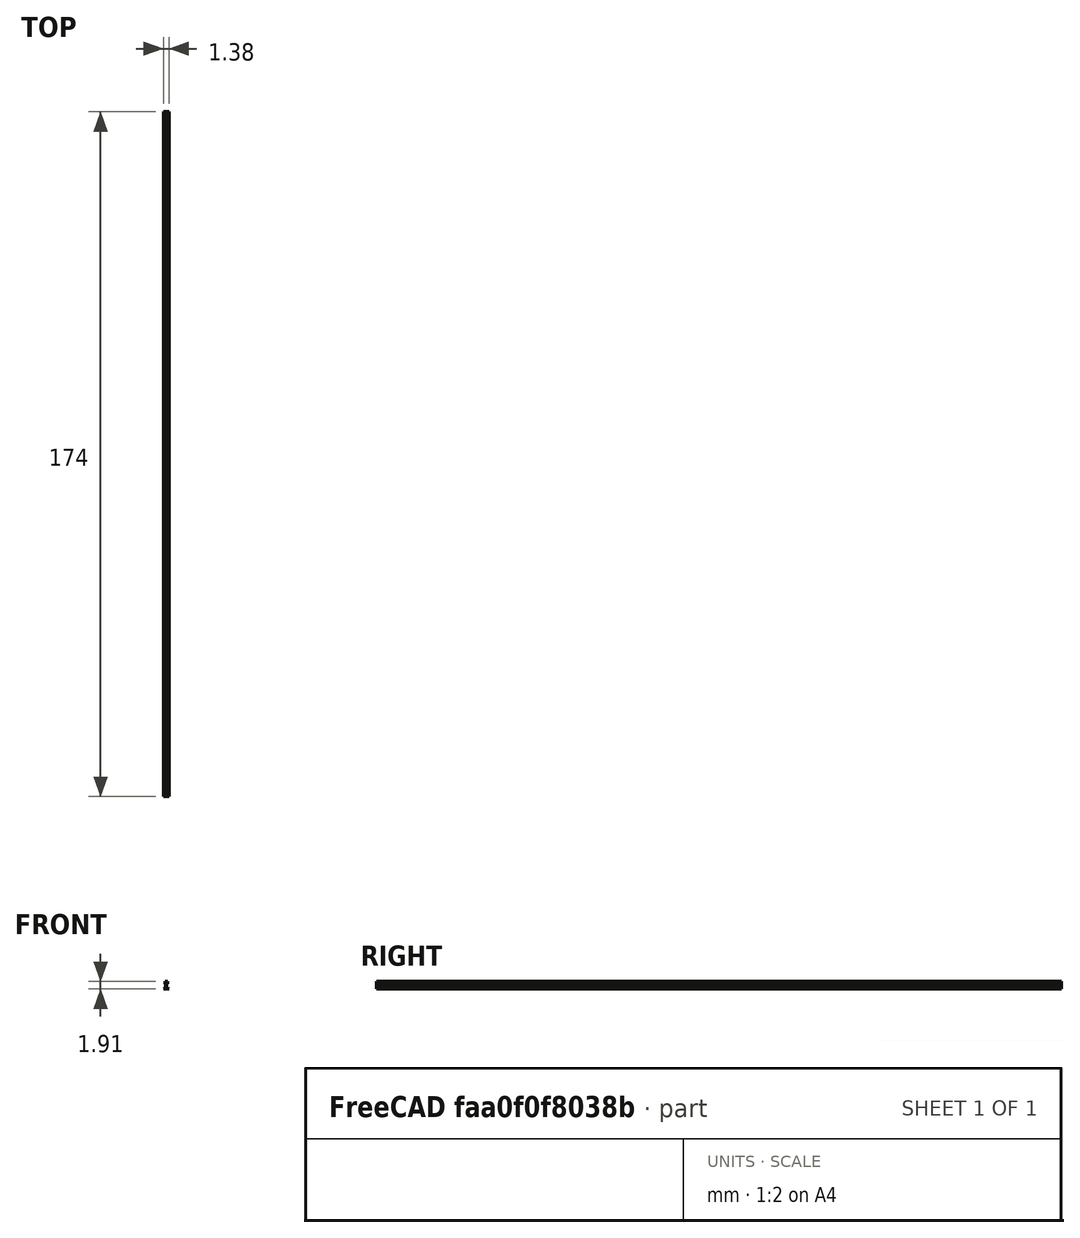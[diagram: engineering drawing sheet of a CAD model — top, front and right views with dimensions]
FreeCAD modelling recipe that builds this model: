
FCSTD DOCUMENT  (FreeCAD 0.18R16131 (Git))
Label: code75-flat-bottom-174mm
License: All rights reserved
LicenseURL: http://en.wikipedia.org/wiki/All_rights_reserved
objects: Sketcher::SketchObject×1, PartDesign::Pad×1, PartDesign::Body×1
note: 4 computed .brp shape members not serialized (recipe doc carries the construction recipe); baked Part::Feature solids carry a one-line shape summary decoded from their .brp

FEATURE [Sketcher::SketchObject] Sketch
  MapMode = 5
  Placement = pos=(0,0,0) rot=(1,0,0;1.5708rad)
  Support = -> [XZ_Plane]
  sketch-geometry (15):
    g0: LineSegment StartX=-0.345 StartY=1.905 StartZ=0 EndX=0.345 EndY=1.905 EndZ=0
    g1: LineSegment [constr] StartX=-0.345 StartY=1.905 StartZ=0 EndX=0 EndY=0 EndZ=0
    g2: LineSegment [constr] StartX=0 StartY=0 StartZ=0 EndX=0.345 EndY=1.905 EndZ=0
    g3: LineSegment StartX=-0.345 StartY=1.905 StartZ=0 EndX=-0.345 EndY=1.355 EndZ=0
    g4: LineSegment StartX=-0.345 StartY=1.355 StartZ=0 EndX=-0.1 EndY=1.215 EndZ=0
    g5: LineSegment StartX=0.345 StartY=1.905 StartZ=0 EndX=0.345 EndY=1.355 EndZ=0
    g6: LineSegment StartX=0.345 StartY=1.355 StartZ=0 EndX=0.1 EndY=1.215 EndZ=0
    g7: LineSegment StartX=-0.1 StartY=1.215 StartZ=0 EndX=-0.1 EndY=0.3 EndZ=0
    g8: LineSegment StartX=0.1 StartY=1.215 StartZ=0 EndX=0.1 EndY=0.3 EndZ=0
    g9: LineSegment StartX=-0.695 StartY=0 StartZ=0 EndX=0.695 EndY=0 EndZ=0
    g10: LineSegment StartX=-0.695 StartY=0 StartZ=0 EndX=-0.695 EndY=0.11 EndZ=0
    g11: LineSegment StartX=0.695 StartY=0 StartZ=0 EndX=0.695 EndY=0.11 EndZ=0
    g12: LineSegment StartX=-0.695 StartY=0.11 StartZ=0 EndX=-0.1 EndY=0.3 EndZ=0
    g13: LineSegment StartX=0.1 StartY=0.3 StartZ=0 EndX=0.695 EndY=0.11 EndZ=0
    g14: LineSegment [constr] StartX=-0.1 StartY=1.215 StartZ=0 EndX=0.1 EndY=1.215 EndZ=0
  constraints (42):
    c: Horizontal(g0)
    c: DistanceY(g-1,g0) = 1.905
    c: DistanceX(g0,g0) = 0.69
    c: Coincident(g1,g0)
    c: Coincident(g1,g-1)
    c: Coincident(g2,g1)
    c: Coincident(g2,g0)
    c: Equal(g2,g1)
    c: Coincident(g3,g0)
    c: Vertical(g3)
    c: Coincident(g4,g3)
    c: Coincident(g5,g0)
    c: Vertical(g5)
    c: Coincident(g6,g5)
    c: Coincident(g7,g4)
    c: Vertical(g7)
    c: Coincident(g8,g6)
    c: Vertical(g8)
    c: Equal(g8,g7)
    c: Equal(g4,g6)
    c: Equal(g3,g5)
    c: PointOnObject(g9,g-1)
    c: Horizontal(g9)
    c: Coincident(g10,g9)
    c: Vertical(g10)
    c: Coincident(g11,g9)
    c: Vertical(g11)
    c: DistanceY(g10,g10) = 0.11
    c: Equal(g10,g11)
    c: DistanceX(g9,g9) = 1.39
    c: Coincident(g12,g10)
    c: Coincident(g12,g7)
    c: Coincident(g13,g8)
    c: Coincident(g13,g11)
    c: Equal(g13,g12)
    c: Coincident(g14,g4)
    c: Coincident(g14,g6)
    c: Horizontal(g14)
    c: DistanceY(g6,g0) = 0.69
    c: DistanceY(g5,g5) = 0.55
    c: DistanceX(g14,g14) = 0.2
    c: DistanceY(g-1,g7) = 0.3
FEATURE [PartDesign::Pad] Pad
  Length = 174
  Length2 = 100
  Midplane = true
  Placement = pos=(0,0,0) rot=(1,0,0;1.5708rad)
  Profile = -> Sketch
  Type = 0
FEATURE [PartDesign::Body] Body
  Group = -> [Sketch,Pad]
  Origin = -> Origin
  Tip = -> Pad
